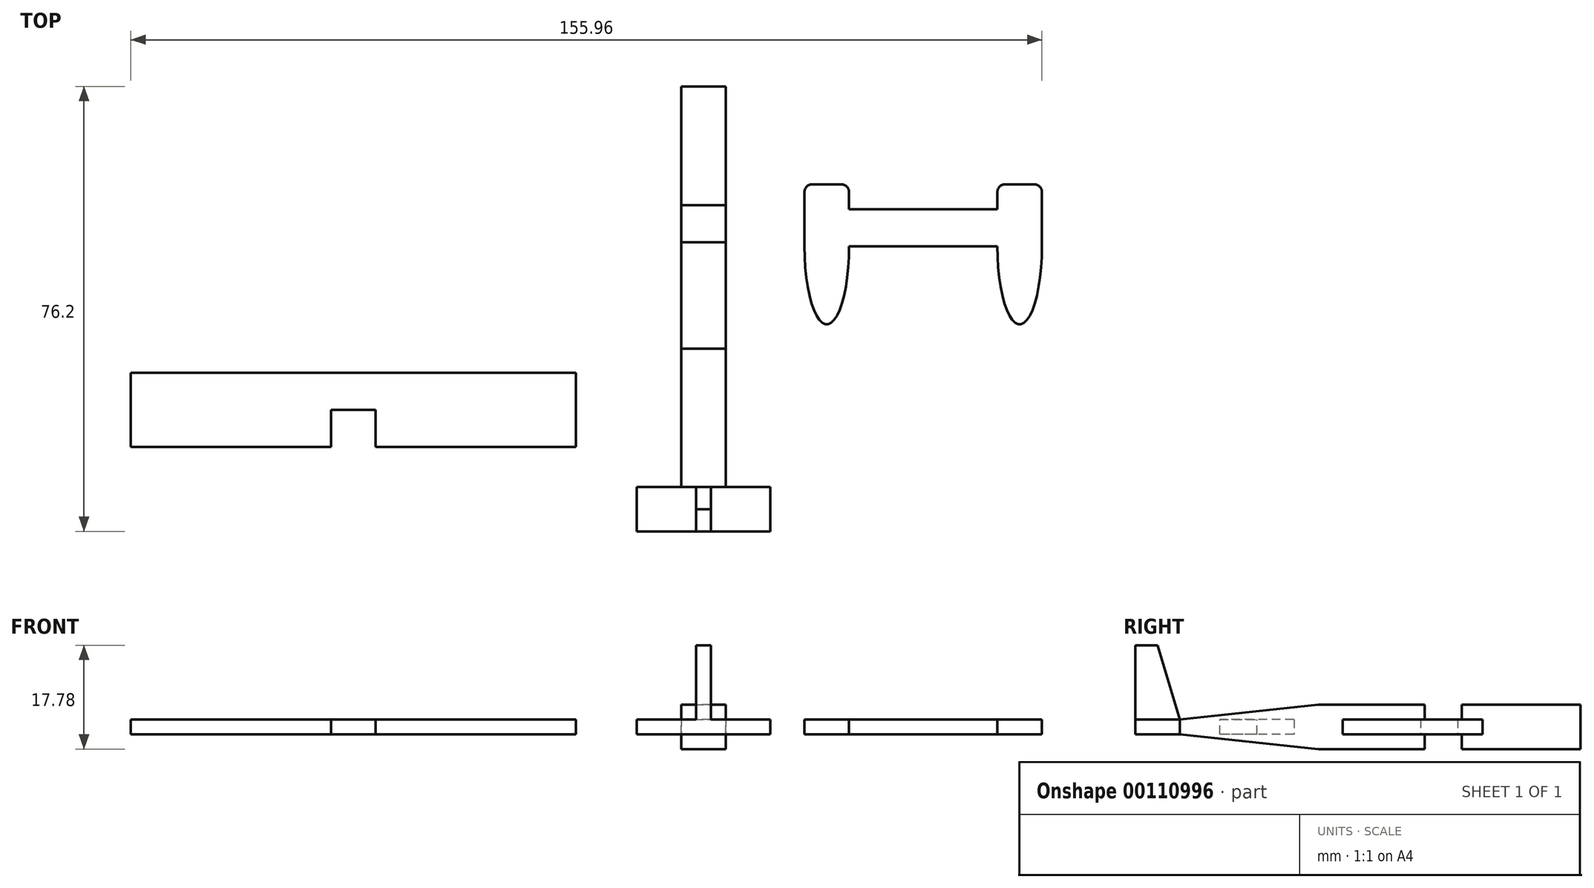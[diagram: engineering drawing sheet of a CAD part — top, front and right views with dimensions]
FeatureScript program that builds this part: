
annotation { "Feature Type Name" : "Feature", "Feature Type Description" : "" }
export const myFeature = defineFeature(function(context is Context, id is Id, definition is map)
    precondition{}
    {
        {
            var Q0;
            Q0=qCreatedBy(makeId("Top.planeOp"),FACE);
            var sketch = newSketch(context, id + "F0", { "sketchPlane" : qUnion([Q0])});
            skLineSegment(sketch, "E0.bottom", {"start": v(-76.2, 12.7) * mm, "end": v(0, 12.7) * mm});
            skLineSegment(sketch, "E0.top", {"start": v(-76.2, 0) * mm, "end": v(0, 0) * mm});
            skLineSegment(sketch, "E0.left", {"start": v(-76.2, 12.7) * mm, "end": v(-76.2, 0) * mm});
            skLineSegment(sketch, "E0.right", {"start": v(0, 12.7) * mm, "end": v(0, 0) * mm});
            skSolve(sketch);
        }
        {
            var Q0;
            Q0=makeQuery(id+"F0.imprint","IMPRINT",FACE,{"disambiguationData":[TD([[makeQuery(id+"F0.imprint","IMPRINT",EDGE,{"derivedFrom":sQuery(id+"F0.wireOp",EDGE,"E0.bottom")}),-1.0]])]});
            extrude(context, id + "F1", {"entities" : qUnion([Q0]), "depth" : 2.54 * mm});
        }
        {
            var Q0;
            Q0=makeQuery(id+"F1.opExtrude","CAP_FACE",FACE,{"disambiguationData":[OSD([sQuery(id+"F0.wireOp",EDGE,"E0.bottom"),sQuery(id+"F0.wireOp",EDGE,"E0.top"),sQuery(id+"F0.wireOp",EDGE,"E0.left"),sQuery(id+"F0.wireOp",EDGE,"E0.right")])],"isStart":false});
            var sketch = newSketch(context, id + "F2", { "sketchPlane" : qUnion([Q0])});
            skLineSegment(sketch, "E1", {"start": v(-38.1, 12.7) * mm, "end": v(-38.1, 0) * mm, "construction": true});
            skLineSegment(sketch, "E2.bottom", {"start": v(-41.91, 0) * mm, "end": v(-34.3, 0) * mm});
            skLineSegment(sketch, "E2.top", {"start": v(-41.91, 6.35) * mm, "end": v(-34.3, 6.35) * mm});
            skLineSegment(sketch, "E2.left", {"start": v(-41.91, 0) * mm, "end": v(-41.91, 6.35) * mm});
            skLineSegment(sketch, "E2.right", {"start": v(-34.3, 0) * mm, "end": v(-34.3, 6.35) * mm});
            skSolve(sketch);
        }
        {
            var Q0;
            Q0=makeQuery(id+"F2.imprint","IMPRINT",FACE,{"disambiguationData":[TD([[makeQuery(id+"F2.imprint","IMPRINT",EDGE,{"derivedFrom":sQuery(id+"F2.wireOp",EDGE,"E2.bottom")}),1.0]])]});
            extrude(context, id + "F3", {"entities" : qUnion([Q0]), "operationType" : NewBodyOperationType.REMOVE, "endBound" : BoundingType.UP_TO_NEXT, "oppositeDirection" : true, "depth" : 25.4 * mm});
        }
        {
            var Q0;
            Q0=qCreatedBy(makeId("Top.planeOp"),FACE);
            var sketch = newSketch(context, id + "F4", { "sketchPlane" : qUnion([Q0])});
            skLineSegment(sketch, "E3.bottom", {"start": v(18, 61.76) * mm, "end": v(25.63, 61.76) * mm});
            skLineSegment(sketch, "E3.top", {"start": v(18, -14.44) * mm, "end": v(25.63, -14.44) * mm});
            skLineSegment(sketch, "E3.left", {"start": v(18, 61.76) * mm, "end": v(18, -14.44) * mm});
            skLineSegment(sketch, "E3.right", {"start": v(25.63, 61.76) * mm, "end": v(25.63, -14.44) * mm});
            skSolve(sketch);
        }
        {
            var Q0;
            Q0=makeQuery(id+"F4.imprint","IMPRINT",FACE,{"disambiguationData":[TD([[makeQuery(id+"F4.imprint","IMPRINT",EDGE,{"derivedFrom":sQuery(id+"F4.wireOp",EDGE,"E3.bottom")}),-1.0]])]});
            extrude(context, id + "F5", {"entities" : qUnion([Q0]), "depth" : 2.54 * mm});
        }
        {
            var Q0;
            Q0=makeQuery(id+"F5.opExtrude","CAP_FACE",FACE,{"disambiguationData":[OSD([sQuery(id+"F4.wireOp",EDGE,"E3.bottom"),sQuery(id+"F4.wireOp",EDGE,"E3.top"),sQuery(id+"F4.wireOp",EDGE,"E3.left"),sQuery(id+"F4.wireOp",EDGE,"E3.right")])],"isStart":false});
            var sketch = newSketch(context, id + "F6", { "sketchPlane" : qUnion([Q0])});
            skLineSegment(sketch, "E4.bottom", {"start": v(18, 61.76) * mm, "end": v(25.63, 61.76) * mm});
            skLineSegment(sketch, "E4.top", {"start": v(18, 41.44) * mm, "end": v(25.63, 41.44) * mm});
            skLineSegment(sketch, "E4.left", {"start": v(18, 61.76) * mm, "end": v(18, 41.44) * mm});
            skLineSegment(sketch, "E4.right", {"start": v(25.63, 61.76) * mm, "end": v(25.63, 41.44) * mm});
            skLineSegment(sketch, "E5.bottom", {"start": v(18, 35.09) * mm, "end": v(25.63, 35.09) * mm});
            skLineSegment(sketch, "E5.top", {"start": v(18, -14.44) * mm, "end": v(25.63, -14.44) * mm});
            skLineSegment(sketch, "E5.left", {"start": v(18, 35.09) * mm, "end": v(18, -14.44) * mm});
            skLineSegment(sketch, "E5.right", {"start": v(25.63, 35.09) * mm, "end": v(25.63, -14.44) * mm});
            skSolve(sketch);
        }
        {
            var Q0;
            Q0=makeQuery(id+"F6.imprint","IMPRINT",FACE,{"disambiguationData":[TD([[makeQuery(id+"F6.imprint","IMPRINT",EDGE,{"derivedFrom":sQuery(id+"F6.wireOp",EDGE,"E4.bottom")}),-1.0]])]});
            var Q1;
            Q1=makeQuery(id+"F6.imprint","IMPRINT",FACE,{"disambiguationData":[TD([[makeQuery(id+"F6.imprint","IMPRINT",EDGE,{"derivedFrom":sQuery(id+"F6.wireOp",EDGE,"E5.bottom")}),-1.0]])]});
            extrude(context, id + "F7", {"entities" : qUnion([Q0, Q1]), "operationType" : NewBodyOperationType.ADD, "depth" : 2.54 * mm});
        }
        {
            var Q0;
            Q0=makeQuery(id+"F5.opExtrude","CAP_FACE",FACE,{"disambiguationData":[OSD([sQuery(id+"F4.wireOp",EDGE,"E3.bottom"),sQuery(id+"F4.wireOp",EDGE,"E3.top"),sQuery(id+"F4.wireOp",EDGE,"E3.left"),sQuery(id+"F4.wireOp",EDGE,"E3.right")])],"isStart":true});
            var sketch = newSketch(context, id + "F8", { "sketchPlane" : qUnion([Q0])});
            skLineSegment(sketch, "E6.bottom", {"start": v(25.63, -61.76) * mm, "end": v(18, -61.76) * mm});
            skLineSegment(sketch, "E6.top", {"start": v(25.63, -41.44) * mm, "end": v(18, -41.44) * mm});
            skLineSegment(sketch, "E6.left", {"start": v(25.63, -61.76) * mm, "end": v(25.63, -41.44) * mm});
            skLineSegment(sketch, "E6.right", {"start": v(18, -61.76) * mm, "end": v(18, -41.44) * mm});
            skLineSegment(sketch, "E7.bottom", {"start": v(25.63, -35.09) * mm, "end": v(18, -35.09) * mm});
            skLineSegment(sketch, "E7.top", {"start": v(25.63, 14.44) * mm, "end": v(18, 14.44) * mm});
            skLineSegment(sketch, "E7.left", {"start": v(25.63, -35.09) * mm, "end": v(25.63, 14.44) * mm});
            skLineSegment(sketch, "E7.right", {"start": v(18, -35.09) * mm, "end": v(18, 14.44) * mm});
            skSolve(sketch);
        }
        {
            var Q0;
            Q0=makeQuery(id+"F8.imprint","IMPRINT",FACE,{"disambiguationData":[TD([[makeQuery(id+"F8.imprint","IMPRINT",EDGE,{"derivedFrom":sQuery(id+"F8.wireOp",EDGE,"E6.bottom")}),1.0]])]});
            var Q1;
            Q1=makeQuery(id+"F8.imprint","IMPRINT",FACE,{"disambiguationData":[TD([[makeQuery(id+"F8.imprint","IMPRINT",EDGE,{"derivedFrom":sQuery(id+"F8.wireOp",EDGE,"E7.bottom")}),-1.0]])]});
            extrude(context, id + "F9", {"entities" : qUnion([Q0, Q1]), "operationType" : NewBodyOperationType.ADD, "depth" : 2.54 * mm});
        }
        {
            var Q0;
            Q0=qCreatedBy(makeId("Top.planeOp"),FACE);
            var sketch = newSketch(context, id + "F10", { "sketchPlane" : qUnion([Q0])});
            skLineSegment(sketch, "E8.bottom", {"start": v(46.74, 40.7) * mm, "end": v(72.14, 40.7) * mm});
            skLineSegment(sketch, "E8.top", {"start": v(46.74, 34.35) * mm, "end": v(72.14, 34.35) * mm});
            skLineSegment(sketch, "E8.left", {"start": v(46.74, 40.7) * mm, "end": v(46.74, 34.35) * mm});
            skLineSegment(sketch, "E8.right", {"start": v(72.14, 40.7) * mm, "end": v(72.14, 34.35) * mm});
            skLineSegment(sketch, "E9", {"start": v(59.44, 40.7) * mm, "end": v(59.44, 34.35) * mm, "construction": true});
            skLineSegment(sketch, "E10.bottom", {"start": v(40.39, 44.96) * mm, "end": v(45.47, 44.96) * mm});
            skLineSegment(sketch, "E10.left", {"start": v(39.12, 43.7) * mm, "end": v(39.12, 34.35) * mm});
            skLineSegment(sketch, "E10.right", {"start": v(46.74, 43.7) * mm, "end": v(46.74, 34.35) * mm});
            skArc(sketch, "E11.filletArc", {"start": v(40.39, 44.96) * mm, "mid": v(39.49, 44.59) * mm, "end": v(39.12, 43.7) * mm});
            skArc(sketch, "E12.filletArc", {"start": v(46.74, 43.7) * mm, "mid": v(46.36, 44.59) * mm, "end": v(45.47, 44.96) * mm});
            skEllipticalArc(sketch, "E13", {});
            skPoint(sketch, "E13.centerSnap0", {"position": v(39.12, 34.35) * mm});
            skEllipticalArc(sketch, "E14.MirrorCS", {});
            skLineSegment(sketch, "E15.MirrorCS", {"start": v(79.76, 43.7) * mm, "end": v(79.76, 34.35) * mm});
            skArc(sketch, "E16.MirrorCS", {"start": v(78.49, 44.96) * mm, "mid": v(79.38, 44.59) * mm, "end": v(79.76, 43.7) * mm});
            skLineSegment(sketch, "E17.MirrorCS", {"start": v(78.49, 44.96) * mm, "end": v(73.4, 44.96) * mm});
            skArc(sketch, "E18.MirrorCS", {"start": v(72.14, 43.7) * mm, "mid": v(72.5, 44.59) * mm, "end": v(73.4, 44.96) * mm});
            skLineSegment(sketch, "E19.MirrorCS", {"start": v(72.14, 43.7) * mm, "end": v(72.14, 34.35) * mm});
            const initialGuessF10  = {"E13": [0.04292669042742721, 0.03435068216156806, 0, -1, 0.013335, 0.00381, 4.71238898038469, 1.5707963267948966], "E14.MirrorCS": [0.07594669042742723, 0.03435068216156806, 0, -1, 0.013335, 0.00381, 4.71238898038469, 1.5707963267948966]};
            skSetInitialGuess(sketch, initialGuessF10);
            skSolve(sketch);
        }
        {
            var Q0;
            Q0=makeQuery(id+"F10.imprint","IMPRINT",FACE,{"disambiguationData":[TD([[makeQuery(id+"F10.imprint","IMPRINT",EDGE,{"derivedFrom":sQuery(id+"F10.wireOp",EDGE,"E8.bottom")}),-1.0]])]});
            var Q1;
            Q1=makeQuery(id+"F10.imprint","IMPRINT",FACE,{"disambiguationData":[TD([[makeQuery(id+"F10.imprint","IMPRINT",EDGE,{"derivedFrom":sQuery(id+"F10.wireOp",EDGE,"E10.bottom")}),-1.0]])]});
            var Q2;
            {var subQ0=sQuery(id+"F10.wireOp",EDGE,"E14.MirrorCS");Q2=makeQuery(id+"F10.imprint","IMPRINT",FACE,{"disambiguationData":[TD([[makeQuery(id+"F10.imprint","IMPRINT",EDGE,{"derivedFrom":subQ0}),1.0]])]});}
            extrude(context, id + "F11", {"entities" : qUnion([Q0, Q1, Q2]), "depth" : 2.54 * mm});
        }
        {
            var Q0;
            Q0=qCreatedBy(makeId("Top.planeOp"),FACE);
            var sketch = newSketch(context, id + "F12", { "sketchPlane" : qUnion([Q0])});
            skLineSegment(sketch, "E20.bottom", {"start": v(10.39, -14.44) * mm, "end": v(33.25, -14.44) * mm});
            skLineSegment(sketch, "E20.top", {"start": v(10.39, -6.82) * mm, "end": v(33.25, -6.82) * mm});
            skLineSegment(sketch, "E20.left", {"start": v(10.39, -14.44) * mm, "end": v(10.39, -6.82) * mm});
            skLineSegment(sketch, "E20.right", {"start": v(33.25, -14.44) * mm, "end": v(33.25, -6.82) * mm});
            skSolve(sketch);
        }
        {
            var Q0;
            Q0=makeQuery(id+"F12.imprint","IMPRINT",FACE,{"disambiguationData":[TD([[makeQuery(id+"F12.imprint","IMPRINT",EDGE,{"derivedFrom":sQuery(id+"F12.wireOp",EDGE,"E20.bottom")}),1.0]])]});
            extrude(context, id + "F13", {"entities" : qUnion([Q0]), "operationType" : NewBodyOperationType.ADD, "depth" : 2.54 * mm});
        }
        {
            var Q0;
            Q0=qCreatedBy(makeId("Top.planeOp"),FACE);
            var sketch = newSketch(context, id + "F14", { "sketchPlane" : qUnion([Q0])});
            skLineSegment(sketch, "E21.bottom", {"start": v(20.55, -6.82) * mm, "end": v(23.09, -6.82) * mm});
            skLineSegment(sketch, "E21.top", {"start": v(20.55, -14.44) * mm, "end": v(23.09, -14.44) * mm});
            skLineSegment(sketch, "E21.left", {"start": v(20.55, -6.82) * mm, "end": v(20.55, -14.44) * mm});
            skLineSegment(sketch, "E21.right", {"start": v(23.09, -6.82) * mm, "end": v(23.09, -14.44) * mm});
            skSolve(sketch);
        }
        {
            var Q0;
            Q0 = qSketchRegion(id + "F14", true);
            extrude(context, id + "F15", {"entities" : qUnion([Q0]), "operationType" : NewBodyOperationType.ADD, "depth" : 15.24 * mm});
        }
        {
            var Q0;
            Q0=makeQuery(id+"F9.boolean.opBoolean","MERGE",FACE,{"derivedFrom":[makeQuery(id+"F7.boolean.opBoolean","MERGE",FACE,{"derivedFrom":[makeQuery(id+"F5.opExtrude","SWEPT_FACE",FACE,{"disambiguationData":[OSD([sQuery(id+"F4.wireOp",EDGE,"E3.left")])]}),makeQuery(id+"F7.opExtrude","SWEPT_FACE",FACE,{"disambiguationData":[OSD([sQuery(id+"F6.wireOp",EDGE,"E4.left")])]}),makeQuery(id+"F7.opExtrude","SWEPT_FACE",FACE,{"disambiguationData":[OSD([sQuery(id+"F6.wireOp",EDGE,"E5.left")])]})]}),makeQuery(id+"F9.opExtrude","SWEPT_FACE",FACE,{"disambiguationData":[OSD([sQuery(id+"F8.wireOp",EDGE,"E6.right")])]}),makeQuery(id+"F9.opExtrude","SWEPT_FACE",FACE,{"disambiguationData":[OSD([sQuery(id+"F8.wireOp",EDGE,"E7.right")])]})]});
            var sketch = newSketch(context, id + "F16", { "sketchPlane" : qUnion([Q0])});
            skLineSegment(sketch, "E22", {"start": v(14.44, -2.54) * mm, "end": v(14.44, 0) * mm});
            skLineSegment(sketch, "E23", {"start": v(14.44, 0) * mm, "end": v(6.82, 0) * mm});
            skLineSegment(sketch, "E24", {"start": v(6.82, 0) * mm, "end": v(-16.86, -2.54) * mm});
            skLineSegment(sketch, "E25", {"start": v(-16.86, -2.54) * mm, "end": v(14.44, -2.54) * mm});
            skSolve(sketch);
        }
        {
            var Q0;
            Q0=makeQuery(id+"F16.imprint","IMPRINT",FACE,{"disambiguationData":[TD([[makeQuery(id+"F16.imprint","IMPRINT",EDGE,{"derivedFrom":sQuery(id+"F16.wireOp",EDGE,"E22")}),-1.0]])]});
            extrude(context, id + "F17", {"entities" : qUnion([Q0]), "operationType" : NewBodyOperationType.REMOVE, "endBound" : BoundingType.UP_TO_NEXT, "oppositeDirection" : true, "depth" : 25.4 * mm});
        }
        {
            var Q0;
            Q0=makeQuery(id+"F9.boolean.opBoolean","MERGE",FACE,{"derivedFrom":[makeQuery(id+"F7.boolean.opBoolean","MERGE",FACE,{"derivedFrom":[makeQuery(id+"F5.opExtrude","SWEPT_FACE",FACE,{"disambiguationData":[OSD([sQuery(id+"F4.wireOp",EDGE,"E3.left")])]}),makeQuery(id+"F7.opExtrude","SWEPT_FACE",FACE,{"disambiguationData":[OSD([sQuery(id+"F6.wireOp",EDGE,"E4.left")])]}),makeQuery(id+"F7.opExtrude","SWEPT_FACE",FACE,{"disambiguationData":[OSD([sQuery(id+"F6.wireOp",EDGE,"E5.left")])]})]}),makeQuery(id+"F9.opExtrude","SWEPT_FACE",FACE,{"disambiguationData":[OSD([sQuery(id+"F8.wireOp",EDGE,"E6.right")])]}),makeQuery(id+"F9.opExtrude","SWEPT_FACE",FACE,{"disambiguationData":[OSD([sQuery(id+"F8.wireOp",EDGE,"E7.right")])]})]});
            var sketch = newSketch(context, id + "F18", { "sketchPlane" : qUnion([Q0])});
            skLineSegment(sketch, "E26.bottom", {"start": v(14.44, 5.08) * mm, "end": v(6.82, 5.08) * mm});
            skLineSegment(sketch, "E26.top", {"start": v(14.44, 2.54) * mm, "end": v(6.82, 2.54) * mm});
            skLineSegment(sketch, "E26.left", {"start": v(14.44, 5.08) * mm, "end": v(14.44, 2.54) * mm});
            skLineSegment(sketch, "E26.right", {"start": v(6.82, 5.08) * mm, "end": v(6.82, 2.54) * mm});
            skSolve(sketch);
        }
        {
            var Q0;
            Q0=makeQuery(id+"F18.imprint","IMPRINT",FACE,{"disambiguationData":[TD([[makeQuery(id+"F18.imprint","IMPRINT",EDGE,{"derivedFrom":sQuery(id+"F18.wireOp",EDGE,"E26.bottom")}),-1.0]])]});
            extrude(context, id + "F19", {"entities" : qUnion([Q0]), "operationType" : NewBodyOperationType.REMOVE, "oppositeDirection" : true, "depth" : 2.54 * mm});
        }
        {
            var Q0;
            Q0=makeQuery(id+"F9.boolean.opBoolean","MERGE",FACE,{"derivedFrom":[makeQuery(id+"F7.boolean.opBoolean","MERGE",FACE,{"derivedFrom":[makeQuery(id+"F5.opExtrude","SWEPT_FACE",FACE,{"disambiguationData":[OSD([sQuery(id+"F4.wireOp",EDGE,"E3.right")])]}),makeQuery(id+"F7.opExtrude","SWEPT_FACE",FACE,{"disambiguationData":[OSD([sQuery(id+"F6.wireOp",EDGE,"E4.right")])]}),makeQuery(id+"F7.opExtrude","SWEPT_FACE",FACE,{"disambiguationData":[OSD([sQuery(id+"F6.wireOp",EDGE,"E5.right")])]})]}),makeQuery(id+"F9.opExtrude","SWEPT_FACE",FACE,{"disambiguationData":[OSD([sQuery(id+"F8.wireOp",EDGE,"E6.left")])]}),makeQuery(id+"F9.opExtrude","SWEPT_FACE",FACE,{"disambiguationData":[OSD([sQuery(id+"F8.wireOp",EDGE,"E7.left")])]})]});
            var sketch = newSketch(context, id + "F20", { "sketchPlane" : qUnion([Q0])});
            skLineSegment(sketch, "E27.bottom", {"start": v(-14.44, 5.08) * mm, "end": v(-6.82, 5.08) * mm});
            skLineSegment(sketch, "E27.top", {"start": v(-14.44, 2.54) * mm, "end": v(-6.82, 2.54) * mm});
            skLineSegment(sketch, "E27.left", {"start": v(-14.44, 5.08) * mm, "end": v(-14.44, 2.54) * mm});
            skLineSegment(sketch, "E27.right", {"start": v(-6.82, 5.08) * mm, "end": v(-6.82, 2.54) * mm});
            skSolve(sketch);
        }
        {
            var Q0;
            Q0=makeQuery(id+"F20.imprint","IMPRINT",FACE,{"disambiguationData":[TD([[makeQuery(id+"F20.imprint","IMPRINT",EDGE,{"derivedFrom":sQuery(id+"F20.wireOp",EDGE,"E27.bottom")}),1.0]])]});
            extrude(context, id + "F21", {"entities" : qUnion([Q0]), "operationType" : NewBodyOperationType.REMOVE, "oppositeDirection" : true, "depth" : 2.54 * mm});
        }
        {
            var Q0;
            Q0=makeQuery(id+"F9.boolean.opBoolean","MERGE",FACE,{"derivedFrom":[makeQuery(id+"F7.boolean.opBoolean","MERGE",FACE,{"derivedFrom":[makeQuery(id+"F5.opExtrude","SWEPT_FACE",FACE,{"disambiguationData":[OSD([sQuery(id+"F4.wireOp",EDGE,"E3.left")])]}),makeQuery(id+"F7.opExtrude","SWEPT_FACE",FACE,{"disambiguationData":[OSD([sQuery(id+"F6.wireOp",EDGE,"E4.left")])]}),makeQuery(id+"F7.opExtrude","SWEPT_FACE",FACE,{"disambiguationData":[OSD([sQuery(id+"F6.wireOp",EDGE,"E5.left")])]})]}),makeQuery(id+"F9.opExtrude","SWEPT_FACE",FACE,{"disambiguationData":[OSD([sQuery(id+"F8.wireOp",EDGE,"E6.right")])]}),makeQuery(id+"F9.opExtrude","SWEPT_FACE",FACE,{"disambiguationData":[OSD([sQuery(id+"F8.wireOp",EDGE,"E7.right")])]})]});
            var sketch = newSketch(context, id + "F22", { "sketchPlane" : qUnion([Q0])});
            skLineSegment(sketch, "E28", {"start": v(6.82, 2.54) * mm, "end": v(6.82, 5.08) * mm});
            skLineSegment(sketch, "E29", {"start": v(6.82, 5.08) * mm, "end": v(-16.86, 5.08) * mm});
            skLineSegment(sketch, "E30", {"start": v(-16.86, 5.08) * mm, "end": v(6.82, 2.54) * mm});
            skLineSegment(sketch, "E31", {"start": v(-16.86, -2.54) * mm, "end": v(-16.86, 5.08) * mm, "construction": true});
            skSolve(sketch);
        }
        {
            var Q0;
            Q0=makeQuery(id+"F22.imprint","IMPRINT",FACE,{"disambiguationData":[TD([[makeQuery(id+"F22.imprint","IMPRINT",EDGE,{"derivedFrom":sQuery(id+"F22.wireOp",EDGE,"E28")}),-1.0]])]});
            extrude(context, id + "F23", {"entities" : qUnion([Q0]), "operationType" : NewBodyOperationType.REMOVE, "endBound" : BoundingType.UP_TO_NEXT, "oppositeDirection" : true, "depth" : 25.4 * mm});
        }
        {
            var Q0;
            Q0=makeQuery(id+"F19.boolean.opBoolean","MERGE",FACE,{"derivedFrom":[makeQuery(id+"F15.opExtrude","SWEPT_FACE",FACE,{"disambiguationData":[OSD([sQuery(id+"F14.wireOp",EDGE,"E21.left")])]}),makeQuery(id+"F19.opExtrude","CAP_FACE",FACE,{"disambiguationData":[OSD([sQuery(id+"F18.wireOp",EDGE,"E26.bottom"),sQuery(id+"F18.wireOp",EDGE,"E26.top"),sQuery(id+"F18.wireOp",EDGE,"E26.left"),sQuery(id+"F18.wireOp",EDGE,"E26.right")])],"isStart":false})]});
            var sketch = newSketch(context, id + "F24", { "sketchPlane" : qUnion([Q0])});
            skLineSegment(sketch, "E32", {"start": v(6.82, 2.54) * mm, "end": v(6.82, 15.24) * mm});
            skLineSegment(sketch, "E33", {"start": v(6.82, 15.24) * mm, "end": v(10.63, 15.24) * mm});
            skLineSegment(sketch, "E34", {"start": v(10.63, 15.24) * mm, "end": v(6.82, 2.54) * mm});
            skSolve(sketch);
        }
        {
            var Q0;
            Q0=makeQuery(id+"F24.imprint","IMPRINT",FACE,{"disambiguationData":[TD([[makeQuery(id+"F24.imprint","IMPRINT",EDGE,{"derivedFrom":sQuery(id+"F24.wireOp",EDGE,"E32")}),1.0]])]});
            extrude(context, id + "F25", {"entities" : qUnion([Q0]), "operationType" : NewBodyOperationType.REMOVE, "endBound" : BoundingType.UP_TO_NEXT, "oppositeDirection" : true, "depth" : 25.4 * mm});
        }
    });
